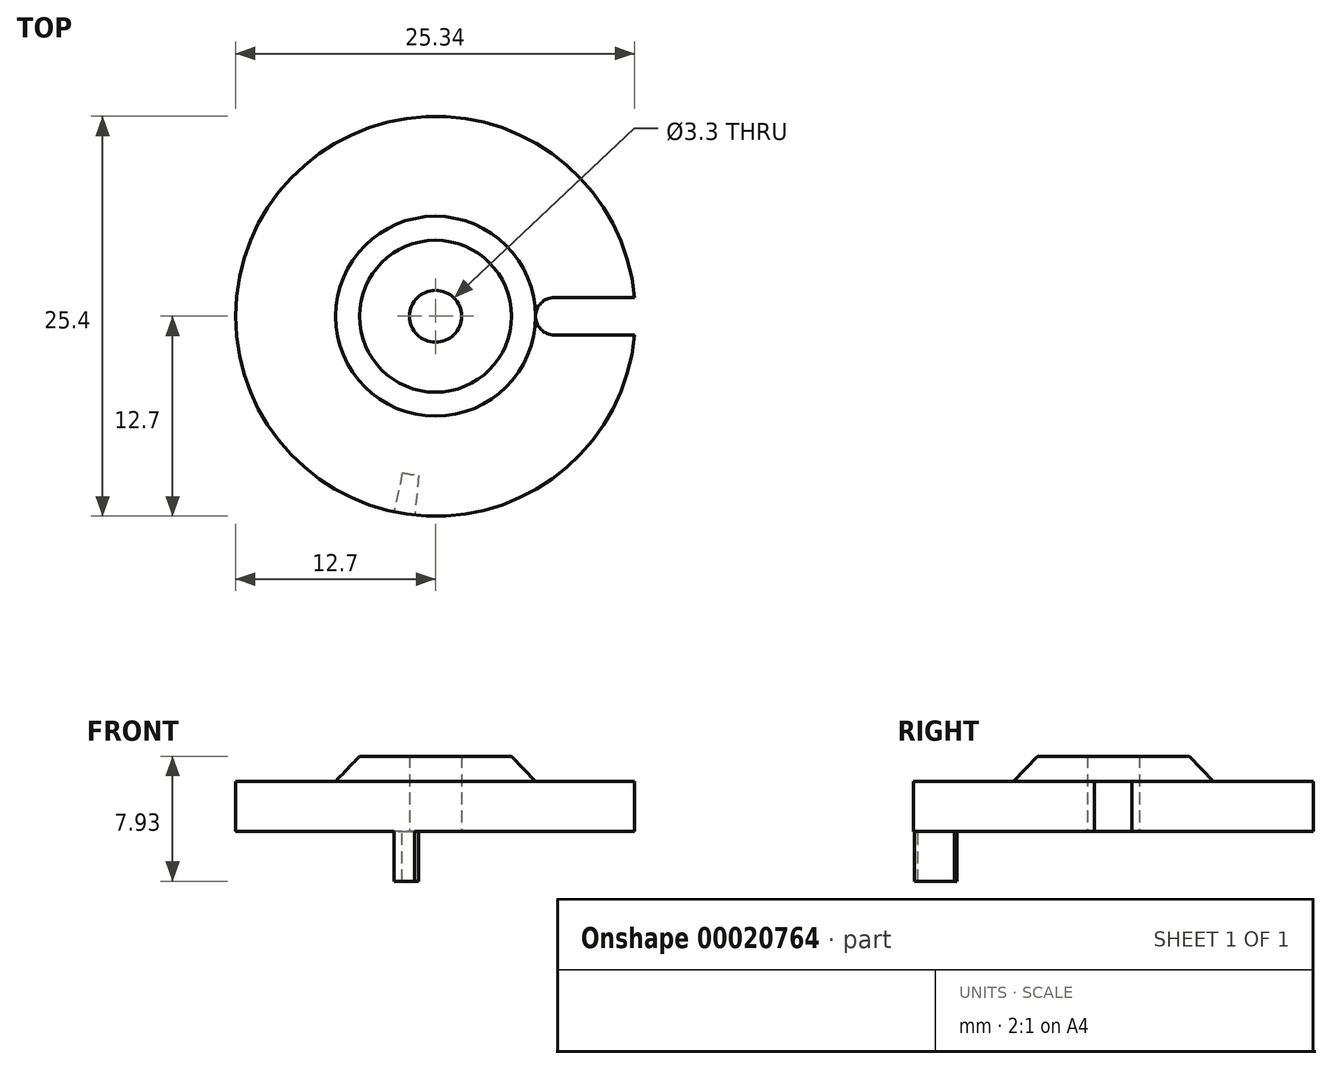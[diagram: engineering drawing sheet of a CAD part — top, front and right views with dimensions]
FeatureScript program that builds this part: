
annotation { "Feature Type Name" : "Feature", "Feature Type Description" : "" }
export const myFeature = defineFeature(function(context is Context, id is Id, definition is map)
    precondition{}
    {
        {
            var Q0;
            Q0=qCreatedBy(makeId("Front.planeOp"),FACE);
            var sketch = newSketch(context, id + "F0", { "sketchPlane" : qUnion([Q0])});
            skLineSegment(sketch, "E0", {"start": v(0, 0) * mm, "end": v(1.65, 0) * mm});
            skLineSegment(sketch, "E1", {"start": v(1.65, 0) * mm, "end": v(1.65, 4.76) * mm});
            skLineSegment(sketch, "E2", {"start": v(1.65, 0) * mm, "end": v(12.7, 0) * mm});
            skLineSegment(sketch, "E3", {"start": v(1.65, 4.76) * mm, "end": v(4.83, 4.76) * mm});
            skLineSegment(sketch, "E4", {"start": v(4.83, 4.76) * mm, "end": v(6.35, 3.17) * mm});
            skLineSegment(sketch, "E5", {"start": v(6.35, 3.18) * mm, "end": v(12.7, 3.18) * mm});
            skLineSegment(sketch, "E6", {"start": v(12.7, 3.18) * mm, "end": v(12.7, 0) * mm});
            skLineSegment(sketch, "E7", {"start": v(0, 0) * mm, "end": v(0, 3.83) * mm});
            skSolve(sketch);
        }
        {
            var Q0;
            Q0=makeQuery(id+"F0.imprint","IMPRINT",FACE,{"disambiguationData":[TD([[makeQuery(id+"F0.imprint","IMPRINT",EDGE,{"derivedFrom":sQuery(id+"F0.wireOp",EDGE,"E1")}),-1.0]])]});
            var Q1;
            Q1=sQuery(id+"F0.wireOp",EDGE,"E7");
            revolve(context, id + "F1", {"entities" : qUnion([Q0]), "axis" : qUnion([Q1]), "revolveType" : RevolveType.FULL});
        }
        {
            var Q0;
            Q0=makeQuery(id+"F1.opRevolve","SWEPT_FACE",FACE,{"disambiguationData":[OSD([sQuery(id+"F0.wireOp",EDGE,"E2")])]});
            var sketch = newSketch(context, id + "F2", { "sketchPlane" : qUnion([Q0])});
            skLineSegment(sketch, "E8", {"start": v(6.35, 0) * mm, "end": v(0, 0) * mm});
            skArc(sketch, "E9", {"start": v(7.54, 1.2) * mm, "mid": v(6.35, 0) * mm, "end": v(7.54, -1.2) * mm});
            skLineSegment(sketch, "E10", {"start": v(7.54, 1.2) * mm, "end": v(12.64, 1.2) * mm});
            skLineSegment(sketch, "E11", {"start": v(7.54, -1.2) * mm, "end": v(12.64, -1.2) * mm});
            skCircle(sketch, "E12.0", {"center": v(0, 0) * mm, "radius": 12.7 * mm});
            skSolve(sketch);
        }
        {
            var Q0;
            {var subQ2=sQuery(id+"F2.wireOp",EDGE,"E10");Q0=makeQuery(id+"F2.imprint","IMPRINT",FACE,{"disambiguationData":[TD([[makeQuery(id+"F2.imprint","IMPRINT",EDGE,{"derivedFrom":subQ2}),-1.0]])]});}
            extrude(context, id + "F3", {"entities" : qUnion([Q0]), "operationType" : NewBodyOperationType.REMOVE, "endBound" : BoundingType.THROUGH_ALL, "oppositeDirection" : true, "depth" : 25.4 * mm});
        }
        {
            var Q0;
            Q0=makeQuery(id+"F1.opRevolve","SWEPT_FACE",FACE,{"disambiguationData":[OSD([sQuery(id+"F0.wireOp",EDGE,"E2")])]});
            var sketch = newSketch(context, id + "F4", { "sketchPlane" : qUnion([Q0])});
            skLineSegment(sketch, "E13", {"start": v(0, 0) * mm, "end": v(-2.64, 12.42) * mm});
            skLineSegment(sketch, "E14", {"start": v(0, 0) * mm, "end": v(-1.33, 12.63) * mm});
            skArc(sketch, "E15", {"start": v(-1.06, 10.1) * mm, "mid": v(-1.59, 10.03) * mm, "end": v(-2.11, 9.94) * mm});
            skSolve(sketch);
        }
        {
            var Q0;
            {var subQ0=sQuery(id+"F4.wireOp",EDGE,"E15");Q0=makeQuery(id+"F4.imprint","IMPRINT",FACE,{"disambiguationData":[TD([[makeQuery(id+"F4.imprint","IMPRINT",EDGE,{"derivedFrom":subQ0}),-1.0]])]});}
            extrude(context, id + "F5", {"entities" : qUnion([Q0]), "operationType" : NewBodyOperationType.ADD, "depth" : 3.17 * mm});
        }
    });
